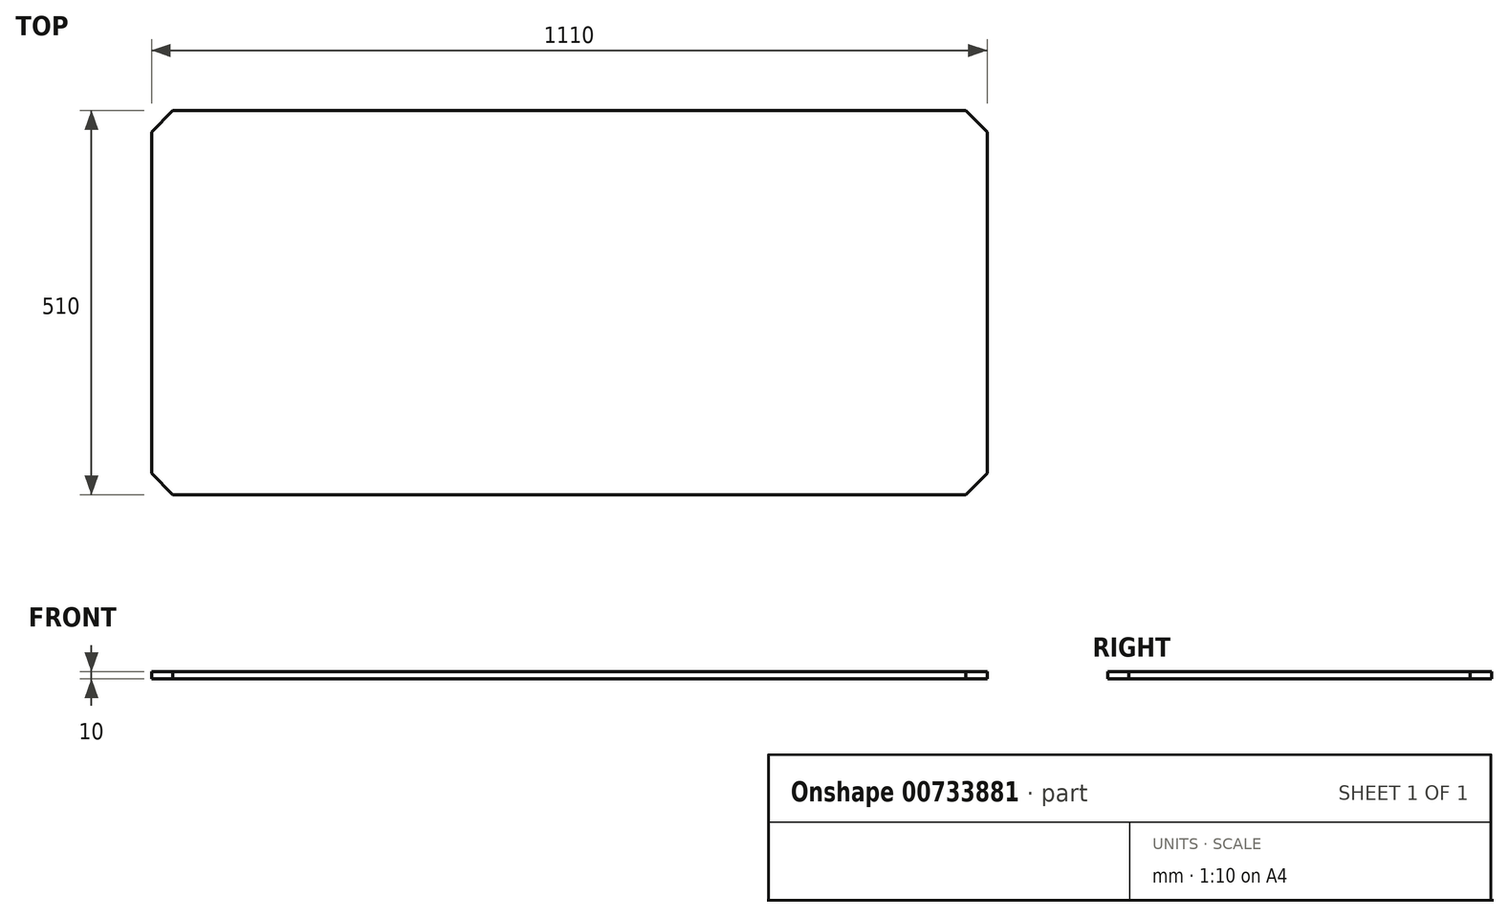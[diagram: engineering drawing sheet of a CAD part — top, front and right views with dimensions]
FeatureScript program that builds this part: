
annotation { "Feature Type Name" : "Feature", "Feature Type Description" : "" }
export const myFeature = defineFeature(function(context is Context, id is Id, definition is map)
    precondition{}
    {
        {
            var Q0;
            Q0=qCreatedBy(makeId("Top.planeOp"),FACE);
            var sketch = newSketch(context, id + "F0", { "sketchPlane" : qUnion([Q0])});
            skLineSegment(sketch, "E0.bottom", {"start": v(-555, 255) * mm, "end": v(555, 255) * mm});
            skLineSegment(sketch, "E0.top", {"start": v(-555, -255) * mm, "end": v(555, -255) * mm});
            skLineSegment(sketch, "E0.left", {"start": v(-555, 255) * mm, "end": v(-555, -255) * mm});
            skLineSegment(sketch, "E0.right", {"start": v(555, 255) * mm, "end": v(555, -255) * mm});
            skPoint(sketch, "E0.middle", {"position": v(0, 0) * mm});
            skLineSegment(sketch, "E1", {"start": v(-555, 226.72) * mm, "end": v(-526.72, 255) * mm});
            skLineSegment(sketch, "E2", {"start": v(526.72, 255) * mm, "end": v(555, 226.72) * mm});
            skLineSegment(sketch, "E3", {"start": v(526.72, -255) * mm, "end": v(555, -226.72) * mm});
            skLineSegment(sketch, "E4", {"start": v(-555, -226.72) * mm, "end": v(-526.72, -255) * mm});
            skSolve(sketch);
        }
        {
            var Q0;
            {var subQ3=sQuery(id+"F0.wireOp",EDGE,"E1");Q0=makeQuery(id+"F0.imprint","IMPRINT",FACE,{"disambiguationData":[TD([[makeQuery(id+"F0.imprint","IMPRINT",EDGE,{"derivedFrom":subQ3}),-1.0]])]});}
            extrude(context, id + "F1", {"entities" : qUnion([Q0]), "depth" : 10 * mm, "offsetDistance" : 25 * mm});
        }
    });
